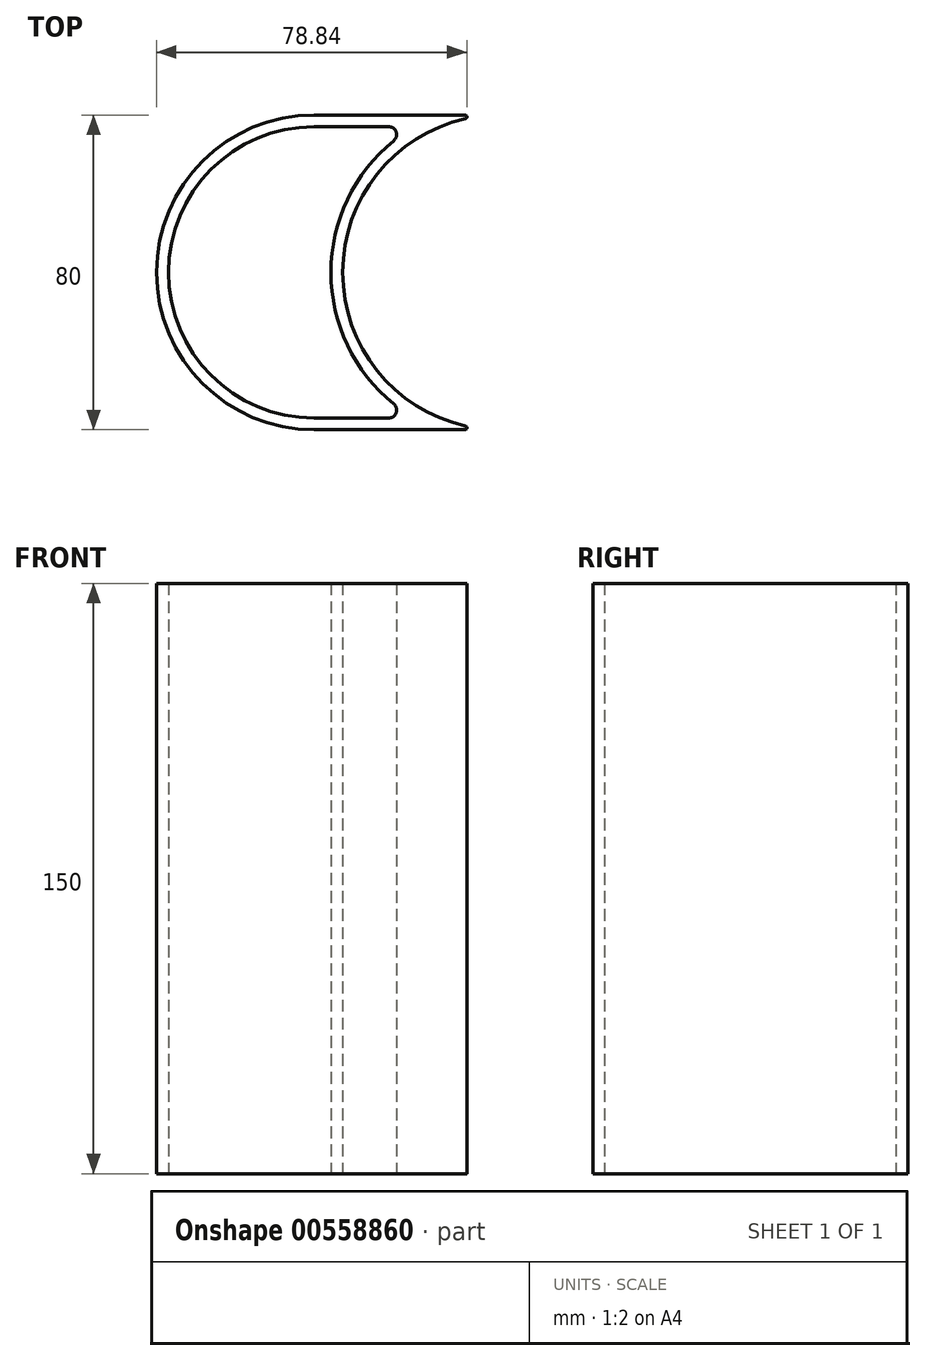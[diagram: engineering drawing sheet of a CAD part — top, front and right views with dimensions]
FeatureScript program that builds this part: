
annotation { "Feature Type Name" : "Feature", "Feature Type Description" : "" }
export const myFeature = defineFeature(function(context is Context, id is Id, definition is map)
    precondition{}
    {
        {
            var Q0;
            Q0=qCreatedBy(makeId("Top.planeOp"),FACE);
            var sketch = newSketch(context, id + "F0", { "sketchPlane" : qUnion([Q0])});
            skArc(sketch, "E0", {"start": v(-62.5, 41.94) * mm, "mid": v(-93.68, 2.93) * mm, "end": v(-62.5, -36.08) * mm});
            skLineSegment(sketch, "E1", {"start": v(-53.68, -44.4) * mm, "end": v(-53.68, 58.56) * mm, "construction": true});
            skArc(sketch, "E2", {"start": v(-100.96, 42.93) * mm, "mid": v(-140.96, 2.93) * mm, "end": v(-100.96, -37.07) * mm});
            skLineSegment(sketch, "E3", {"start": v(-100.96, 42.93) * mm, "end": v(-62.62, 42.93) * mm});
            skLineSegment(sketch, "E4", {"start": v(-100.96, -37.07) * mm, "end": v(-62.62, -37.07) * mm});
            skArc(sketch, "E5.0", {"start": v(-100.96, 39.93) * mm, "mid": v(-137.96, 2.93) * mm, "end": v(-100.96, -34.07) * mm});
            skLineSegment(sketch, "E5.1", {"start": v(-100.96, 39.93) * mm, "end": v(-81.96, 39.93) * mm});
            skArc(sketch, "E5.2", {"start": v(-80.7, 36.37) * mm, "mid": v(-96.68, 2.93) * mm, "end": v(-80.7, -30.52) * mm});
            skLineSegment(sketch, "E5.3", {"start": v(-100.96, -34.07) * mm, "end": v(-81.96, -34.07) * mm});
            skPoint(sketch, "E6.visualSharp", {"position": v(-75.59, 39.93) * mm});
            skArc(sketch, "E6.filletArc", {"start": v(-80.7, 36.37) * mm, "mid": v(-80.07, 38.6) * mm, "end": v(-81.96, 39.93) * mm});
            skPoint(sketch, "E7.visualSharp", {"position": v(-75.59, -34.07) * mm});
            skArc(sketch, "E7.filletArc", {"start": v(-81.96, -34.07) * mm, "mid": v(-80.07, -32.74) * mm, "end": v(-80.7, -30.52) * mm});
            skPoint(sketch, "E8.visualSharp", {"position": v(-53.68, 42.93) * mm});
            skArc(sketch, "E8.filletArc", {"start": v(-62.5, 41.94) * mm, "mid": v(-62.12, 42.48) * mm, "end": v(-62.62, 42.93) * mm});
            skPoint(sketch, "E9.visualSharp", {"position": v(-53.68, -37.07) * mm});
            skArc(sketch, "E9.filletArc", {"start": v(-62.62, -37.07) * mm, "mid": v(-62.12, -36.63) * mm, "end": v(-62.5, -36.08) * mm});
            skSolve(sketch);
        }
        {
            var Q0;
            Q0 = qSketchRegion(id + "F0", true);
            extrude(context, id + "F1", {"entities" : qUnion([Q0]), "depth" : 150 * mm, "offsetDistance" : 25 * mm});
        }
    });
